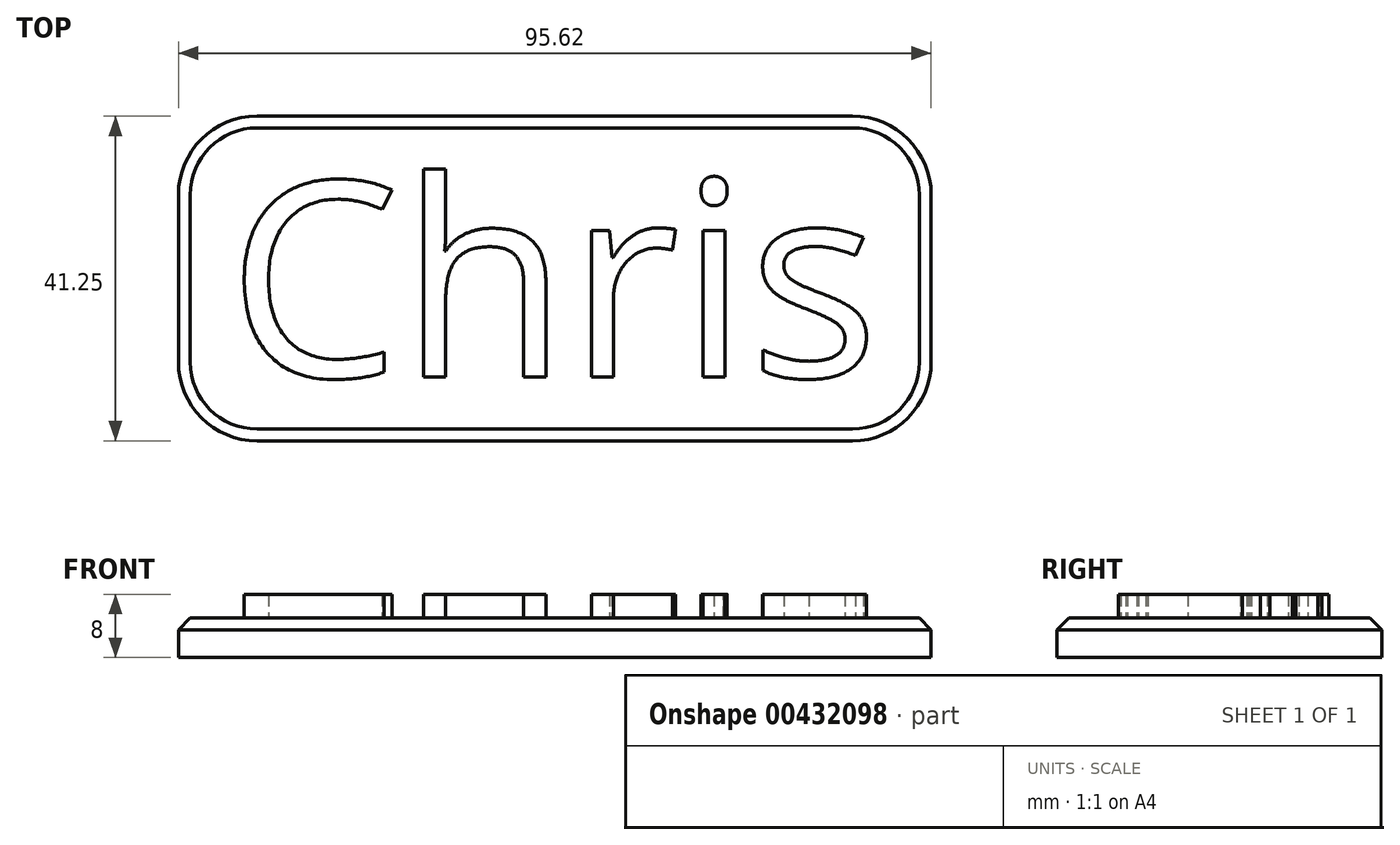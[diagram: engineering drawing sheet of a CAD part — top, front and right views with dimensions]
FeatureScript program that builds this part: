
annotation { "Feature Type Name" : "Feature", "Feature Type Description" : "" }
export const myFeature = defineFeature(function(context is Context, id is Id, definition is map)
    precondition{}
    {
        {
            var Q0;
            Q0=qCreatedBy(makeId("Top.planeOp"),FACE);
            var sketch = newSketch(context, id + "F0", { "sketchPlane" : qUnion([Q0])});
            skLineSegment(sketch, "E0.bottom", {"start": v(-40.81, 17.12) * mm, "end": v(54.81, 17.12) * mm});
            skLineSegment(sketch, "E0.top", {"start": v(-40.81, -24.13) * mm, "end": v(54.81, -24.13) * mm});
            skLineSegment(sketch, "E0.left", {"start": v(-40.81, 17.12) * mm, "end": v(-40.81, -24.13) * mm});
            skLineSegment(sketch, "E0.right", {"start": v(54.81, 17.12) * mm, "end": v(54.81, -24.13) * mm});
            skText(sketch, "E1", { "text": "Chris", "fontName": "OpenSans-Regular.ttf"});
            const initialGuessF0  = {"E1": [-0.03456, -0.016, 1, 0, 0.025]};
            skSetInitialGuess(sketch, initialGuessF0);
            skSolve(sketch);
        }
        {
            var Q0;
            Q0=makeQuery(id+"F0.imprint","IMPRINT",FACE,{"disambiguationData":[TD([[makeQuery(id+"F0.imprint","IMPRINT",EDGE,{"derivedFrom":sQuery(id+"F0.wireOp",EDGE,"E0.bottom")}),-1.0]])]});
            var Q1;
            Q1=makeQuery(id+"F0.imprint","IMPRINT",FACE,{"disambiguationData":[TD([[makeQuery(id+"F0.imprint","IMPRINT",EDGE,{"derivedFrom":sQuery(id+"F0.wireOp",EDGE,"E1.sketch_text.stroke-58")}),-1.0]])]});
            var Q2;
            Q2=makeQuery(id+"F0.imprint","IMPRINT",FACE,{"disambiguationData":[TD([[makeQuery(id+"F0.imprint","IMPRINT",EDGE,{"derivedFrom":sQuery(id+"F0.wireOp",EDGE,"E1.sketch_text.stroke-46")}),-1.0]])]});
            var Q3;
            Q3=makeQuery(id+"F0.imprint","IMPRINT",FACE,{"disambiguationData":[TD([[makeQuery(id+"F0.imprint","IMPRINT",EDGE,{"derivedFrom":sQuery(id+"F0.wireOp",EDGE,"E1.sketch_text.stroke-33")}),-1.0]])]});
            var Q4;
            Q4=makeQuery(id+"F0.imprint","IMPRINT",FACE,{"disambiguationData":[TD([[makeQuery(id+"F0.imprint","IMPRINT",EDGE,{"derivedFrom":sQuery(id+"F0.wireOp",EDGE,"E1.sketch_text.stroke-15")}),-1.0]])]});
            var Q5;
            Q5=makeQuery(id+"F0.imprint","IMPRINT",FACE,{"disambiguationData":[TD([[makeQuery(id+"F0.imprint","IMPRINT",EDGE,{"derivedFrom":sQuery(id+"F0.wireOp",EDGE,"E1.sketch_text.stroke-0")}),-1.0]])]});
            var Q6;
            Q6=makeQuery(id+"F0.imprint","IMPRINT",FACE,{"disambiguationData":[TD([[makeQuery(id+"F0.imprint","IMPRINT",EDGE,{"derivedFrom":sQuery(id+"F0.wireOp",EDGE,"E1.sketch_text.stroke-50")}),-1.0]])]});
            extrude(context, id + "F1", {"entities" : qUnion([Q0, Q1, Q2, Q3, Q4, Q5, Q6]), "depth" : 5 * mm});
        }
        {
            var Q0;
            Q0=makeQuery(id+"F0.imprint","IMPRINT",FACE,{"disambiguationData":[TD([[makeQuery(id+"F0.imprint","IMPRINT",EDGE,{"derivedFrom":sQuery(id+"F0.wireOp",EDGE,"E1.sketch_text.stroke-0")}),-1.0]])]});
            var Q1;
            Q1=makeQuery(id+"F0.imprint","IMPRINT",FACE,{"disambiguationData":[TD([[makeQuery(id+"F0.imprint","IMPRINT",EDGE,{"derivedFrom":sQuery(id+"F0.wireOp",EDGE,"E1.sketch_text.stroke-15")}),-1.0]])]});
            var Q2;
            Q2=makeQuery(id+"F0.imprint","IMPRINT",FACE,{"disambiguationData":[TD([[makeQuery(id+"F0.imprint","IMPRINT",EDGE,{"derivedFrom":sQuery(id+"F0.wireOp",EDGE,"E1.sketch_text.stroke-33")}),-1.0]])]});
            var Q3;
            Q3=makeQuery(id+"F0.imprint","IMPRINT",FACE,{"disambiguationData":[TD([[makeQuery(id+"F0.imprint","IMPRINT",EDGE,{"derivedFrom":sQuery(id+"F0.wireOp",EDGE,"E1.sketch_text.stroke-46")}),-1.0]])]});
            var Q4;
            Q4=makeQuery(id+"F0.imprint","IMPRINT",FACE,{"disambiguationData":[TD([[makeQuery(id+"F0.imprint","IMPRINT",EDGE,{"derivedFrom":sQuery(id+"F0.wireOp",EDGE,"E1.sketch_text.stroke-50")}),-1.0]])]});
            var Q5;
            Q5=makeQuery(id+"F0.imprint","IMPRINT",FACE,{"disambiguationData":[TD([[makeQuery(id+"F0.imprint","IMPRINT",EDGE,{"derivedFrom":sQuery(id+"F0.wireOp",EDGE,"E1.sketch_text.stroke-58")}),-1.0]])]});
            extrude(context, id + "F2", {"entities" : qUnion([Q0, Q1, Q2, Q3, Q4, Q5]), "operationType" : NewBodyOperationType.ADD, "depth" : 8 * mm});
        }
        {
            var Q0;
            Q0=makeQuery(id+"F1.opExtrude","SWEPT_EDGE",EDGE,{"disambiguationData":[OSD([sQuery(id+"F0.wireOp",EDGE,"E0.top"),sQuery(id+"F0.wireOp",EDGE,"E0.left")])]});
            var Q1;
            Q1=makeQuery(id+"F1.opExtrude","SWEPT_EDGE",EDGE,{"disambiguationData":[OSD([sQuery(id+"F0.wireOp",EDGE,"E0.top"),sQuery(id+"F0.wireOp",EDGE,"E0.right")])]});
            var Q2;
            Q2=makeQuery(id+"F1.opExtrude","SWEPT_EDGE",EDGE,{"disambiguationData":[OSD([sQuery(id+"F0.wireOp",EDGE,"E0.bottom"),sQuery(id+"F0.wireOp",EDGE,"E0.right")])]});
            var Q3;
            Q3=makeQuery(id+"F1.opExtrude","SWEPT_EDGE",EDGE,{"disambiguationData":[OSD([sQuery(id+"F0.wireOp",EDGE,"E0.bottom"),sQuery(id+"F0.wireOp",EDGE,"E0.left")])]});
            fillet(context, id + "F3", {"entities" : qUnion([Q0, Q1, Q2, Q3]), "radius" : 10 * mm, "tangentPropagation" : true, "allowEdgeOverflow" : false});
        }
        {
            var Q0;
            Q0=makeQuery(id+"F1.opExtrude","CAP_EDGE",EDGE,{"disambiguationData":[OSD([sQuery(id+"F0.wireOp",EDGE,"E0.top")])],"isStart":false});
            chamfer(context, id + "F4", {"entities" : qUnion([Q0]), "width" : 1.5 * mm, "tangentPropagation" : true});
        }
    });
